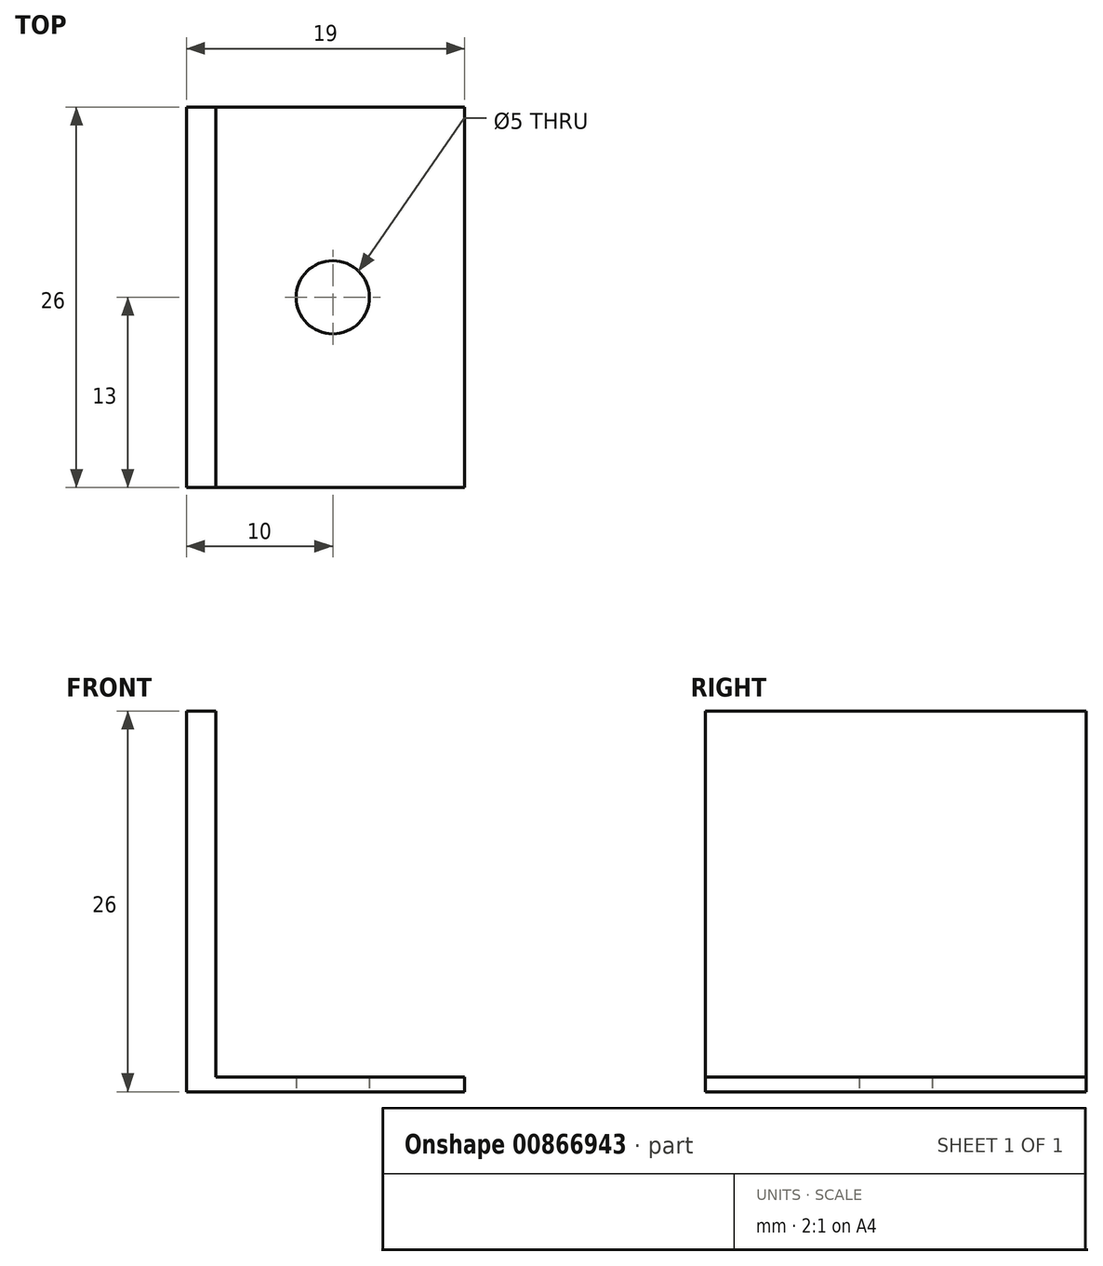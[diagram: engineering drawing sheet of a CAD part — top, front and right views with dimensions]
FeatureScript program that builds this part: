
annotation { "Feature Type Name" : "Feature", "Feature Type Description" : "" }
export const myFeature = defineFeature(function(context is Context, id is Id, definition is map)
    precondition{}
    {
        {
            var Q0;
            Q0=qCreatedBy(makeId("Top.planeOp"),FACE);
            var sketch = newSketch(context, id + "F0", { "sketchPlane" : qUnion([Q0])});
            skLineSegment(sketch, "E0.bottom", {"start": v(0, 0) * mm, "end": v(19, 0) * mm});
            skLineSegment(sketch, "E0.top", {"start": v(0, -26) * mm, "end": v(19, -26) * mm});
            skLineSegment(sketch, "E0.left", {"start": v(0, 0) * mm, "end": v(0, -26) * mm});
            skLineSegment(sketch, "E0.right", {"start": v(19, 0) * mm, "end": v(19, -26) * mm});
            skLineSegment(sketch, "E1", {"start": v(19, -13) * mm, "end": v(10, -13) * mm, "construction": true});
            skCircle(sketch, "E2", {"center": v(10, -13) * mm, "radius": 2.5 * mm});
            skSolve(sketch);
        }
        {
            var Q0;
            Q0=makeQuery(id+"F0.imprint","IMPRINT",FACE,{"disambiguationData":[TD([[makeQuery(id+"F0.imprint","IMPRINT",EDGE,{"derivedFrom":sQuery(id+"F0.wireOp",EDGE,"E0.bottom")}),-1.0]])]});
            extrude(context, id + "F1", {"entities" : qUnion([Q0]), "surfaceOperationType" : NewSurfaceOperationType.ADD, "depth" : 1 * mm, "offsetDistance" : 25 * mm});
        }
        {
            var Q0;
            Q0=makeQuery(id+"F1.opExtrude","CAP_FACE",FACE,{"disambiguationData":[OSD([sQuery(id+"F0.wireOp",EDGE,"E0.bottom"),sQuery(id+"F0.wireOp",EDGE,"E0.top"),sQuery(id+"F0.wireOp",EDGE,"E0.left"),sQuery(id+"F0.wireOp",EDGE,"E0.right"),sQuery(id+"F0.wireOp",EDGE,"E2")])],"isStart":false});
            var sketch = newSketch(context, id + "F2", { "sketchPlane" : qUnion([Q0])});
            skLineSegment(sketch, "E3", {"start": v(0, -26) * mm, "end": v(0, 0) * mm});
            skLineSegment(sketch, "E4", {"start": v(0, 0) * mm, "end": v(2, 0) * mm});
            skLineSegment(sketch, "E5", {"start": v(2, 0) * mm, "end": v(2, -26) * mm});
            skLineSegment(sketch, "E6", {"start": v(2, -26) * mm, "end": v(0, -26) * mm});
            skSolve(sketch);
        }
        {
            var Q0;
            Q0=makeQuery(id+"F2.imprint","IMPRINT",FACE,{"disambiguationData":[TD([[makeQuery(id+"F2.imprint","IMPRINT",EDGE,{"derivedFrom":sQuery(id+"F2.wireOp",EDGE,"E3")}),1.0]])]});
            extrude(context, id + "F3", {"entities" : qUnion([Q0]), "operationType" : NewBodyOperationType.ADD, "depth" : 25 * mm, "offsetDistance" : 25 * mm});
        }
    });
